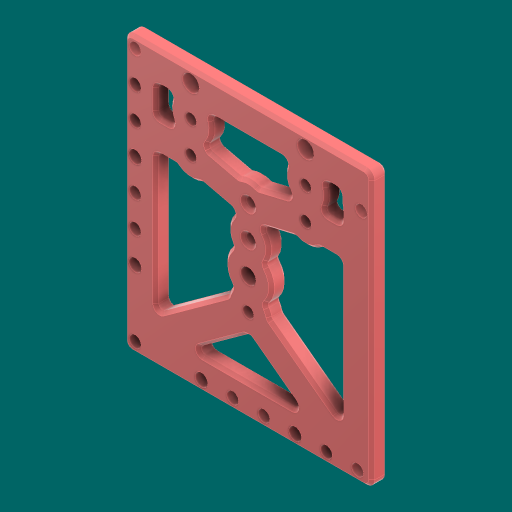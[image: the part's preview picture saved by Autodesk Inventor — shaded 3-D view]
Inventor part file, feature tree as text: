
AUTODESK INVENTOR PART (.ipt)
format: ipt  version: 2023.1 (Build 271208000, 208)  size: 1,139,712 bytes
history: native  units: in
note: dims shown in document units (in); Inventor stores cm internally (conversion verified against a paired STEP export)
features: reference x4, other x4, extrude x2, chamfer x2, sketch x2, fillet x1, projected_geometry x1
ambient origin geometry x8: Origin, YZ Plane, XZ Plane, XY Plane, X Axis, Y Axis, Z Axis, Center Point
bodies: Solid1 (feature_tree)
feature tree (16):
  extrude  "Extrusion1"  Depth=0.18in
  extrude  "Extrusion2"  Depth=0.0625in
  fillet  "Fillet2"  Radius=0.5in
  chamfer  "Chamfer1"  Distance=0.18in
  chamfer  "Chamfer2"  Distance=0.5in
  sketch  "Sketch1"  dims[d0=0.5in d1=0.18in]
  reference  "Reference1"
  reference  "Reference2"
  reference  "Reference3"
  reference  "Reference4"
  sketch  "Sketch2"  dims[d2=0.5in d3=0.18in d4=0.5in d5=0.18in d6=0.5in d7=0.18in d8=0.25in d9=0.5in d10=0.1562in d11=0.5in d12=0.5in d13=0.18in d14=0.25in d15=0.0in d16=0.5in d17=0.25in d18=0.25in d19=0.25in d20=0.25in d21=0.25in d22=0.25in d23=0.25in d24=0.25in d25=0.25in d26=0.25in d27=0.25in d28=0.25in d29=0.5in d30=0.5in d31=0.5in d32=0.5in d34=0.5in d35=0.5in d36=0.0in d37=0.0in d39=0.0625in d40=0.0472in d41=0.125in d42=45.0deg d43=0.0472in d44=0.125in d45=45.0deg]
  projected_geometry  "Projected Loop1"
  other  "<userpath>\Documents\CAD\guardSwerve5\MainAssy.iam"
  other  "MainAssy.iam"
  other  "Baseplate:1"
  other  "DiffCap:1"
